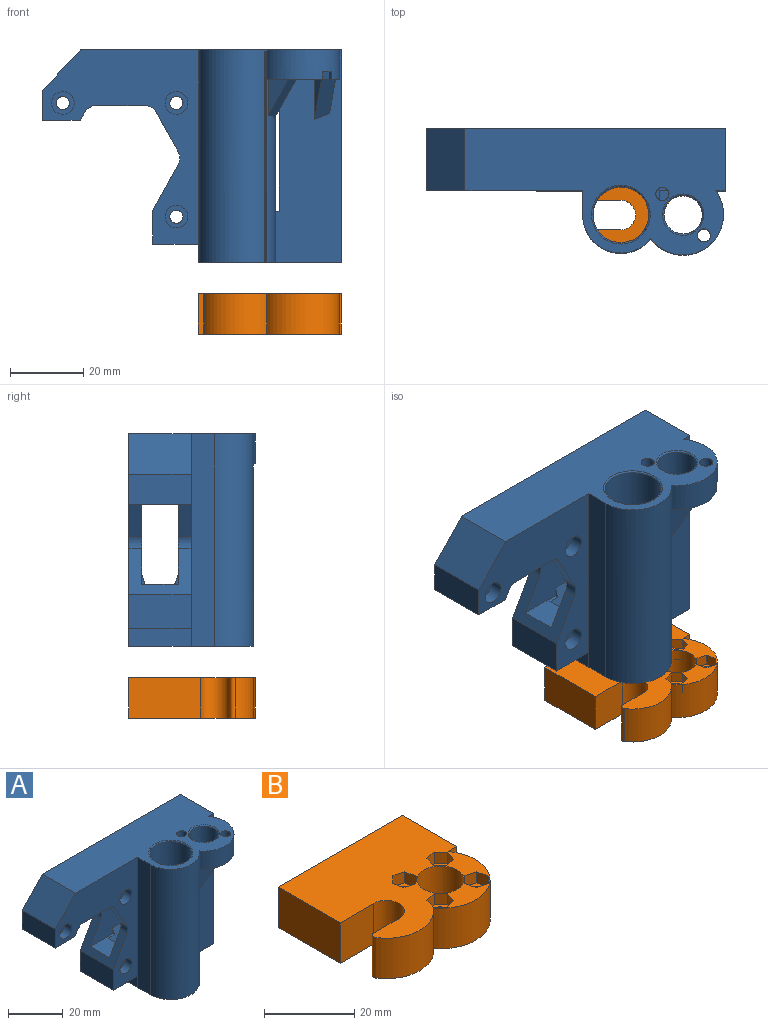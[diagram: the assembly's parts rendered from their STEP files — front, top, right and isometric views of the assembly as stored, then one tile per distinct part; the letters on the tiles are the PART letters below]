
ASSEMBLY  parts=2 mates=1
PART A: 108 faces, bbox 81.5x34.5x58 mm
  f0: cylinder r=10.47mm len=50mm, axis (0,0,1), area 313.5mm2, adj f1,f3,f9,f82,f83,f87,f106
  f1: plane 39x33.98mm, normal (0,0,-1), area 786.5mm2, adj f0,f2,f4,f9,f11,f12,f21,f33
  f2: cylinder r=7.62mm len=57.6mm, axis (0,0,1), area 2698.4mm2, adj f1,f79,f105,f106,f107
  f3: plane 15.16x13.29mm, normal (0,0,-1), area 49.7mm2, adj f0,f5,f9,f80,f82,f83,f87,f89
  f4: plane 58x18.03mm, normal (0,-1,0), area 843.5mm2, adj f1,f5,f8,f9,f10,f21,f37,f38
  f5: cylinder r=11mm len=19.83mm, axis (0,0,1), area 268.6mm2, adj f3,f4,f8,f10,f11,f96,f100,f101
  f6: cylinder r=1.8mm len=6mm, axis (0,0,1), area 67.9mm2, adj f10,f101
  f7: cylinder r=1.8mm len=6mm, axis (0,0,1), area 67.9mm2, adj f10,f90
  f8: plane 13.23x12.97mm, normal (0,0,-1), area 41.4mm2, adj f4,f5,f80,f84,f85,f86,f88,f98
  f9: plane 50x6.5mm, normal (1,0,0), area 316.8mm2, adj f0,f1,f3,f4,f89,f95,f102,f103
  f10: plane 71.05x34.5mm, normal (0,0,1), area 1473.5mm2, adj f4,f5,f6,f7,f11,f12,f21,f34
  f11: cylinder r=10.47mm len=58mm, axis (0,0,1), area 1440.2mm2, adj f1,f5,f10,f78,f105,f107
  f12: plane 58x42.53mm, normal (0,-1,0), area 907.7mm2, adj f1,f10,f13,f14,f15,f27,f28,f29
  f13: plane 17x11.05mm, normal (-0.87,0,-0.49), area 116.3mm2, adj f12,f14,f29,f30,f42,f57,f60,f75
  f14: cylinder r=3.5mm len=3.5mm, axis (0,1,0), area 12.4mm2, adj f12,f13,f15,f57
  f15: plane 17x12.59mm, normal (-0.87,0,0.49), area 132.8mm2, adj f12,f14,f30,f31,f42,f57,f60,f76
  f16: plane 10x3.25mm, normal (1,0,0), area 23.1mm2, adj f38,f55,f56,f57,f60,f75
  f17: plane 30.15x0.91mm, normal (0,0.71,0.71), area 36.2mm2, adj f18,f20,f21,f70,f71
  f18: plane 30.11x2.39mm, normal (0,0,1), area 70.9mm2, adj f17,f19,f21,f70
  f19: plane 30.15x0.91mm, normal (0,-0.71,0.71), area 36.2mm2, adj f18,f20,f21,f70,f71
  f20: cylinder r=4.07mm len=29.1mm, axis (1,0,0), area 618.8mm2, adj f17,f19,f21,f71
  f21: plane 58x17mm, normal (1,0,0), area 620mm2, adj f1,f4,f10,f17,f18,f19,f20,f38
  f22: plane 28x6.57mm, normal (1,0,0), area 108.5mm2, adj f38,f40,f42,f55,f59,f60
  f23: plane 28x6.57mm, normal (-1,0,0), area 108.5mm2, adj f38,f40,f42,f49,f50,f51
  f24: cylinder r=1.8mm len=13.5mm, axis (0,1,0), area 152.7mm2, adj f42,f48
  f25: cylinder r=1.8mm len=13.5mm, axis (0,1,0), area 152.7mm2, adj f42,f46
  f26: cylinder r=1.8mm len=13.5mm, axis (0,1,0), area 152.7mm2, adj f42,f44
  f27: plane 17x1.73mm, normal (0.5,0,-0.87), area 34mm2, adj f12,f28,f41,f42
  f28: plane 17x14.58mm, normal (0,0,-1), area 247.8mm2, adj f12,f27,f29,f42
  f29: cylinder r=3mm len=17mm, axis (0,1,0), area 54.2mm2, adj f12,f13,f28,f42
  f30: cylinder r=3.5mm len=3.5mm, axis (0,1,0), area 12.4mm2, adj f13,f15,f42,f60
  f31: plane 17x9.14mm, normal (-1,0,0), area 155.4mm2, adj f12,f15,f32,f42
  f32: plane 17x12.5mm, normal (0,0,-1), area 212.5mm2, adj f12,f31,f33,f42
  f33: plane 17x5mm, normal (-1,0,0), area 85mm2, adj f1,f12,f32,f42
  f34: plane 17x10.95mm, normal (-0.72,0,0.69), area 257.3mm2, adj f10,f12,f35,f42
  f35: plane 17x8.3mm, normal (-1,0,0), area 141.1mm2, adj f12,f34,f36,f42
  f36: plane 17x10.21mm, normal (0,0,-1), area 173.6mm2, adj f12,f35,f41,f42
  f37: plane 28x6.57mm, normal (1,0,0), area 108.5mm2, adj f4,f38,f40,f56,f57,f58
  f38: plane 41.5x17mm, normal (0,0,-1), area 173.3mm2, adj f4,f16,f21,f22,f23,f37,f39,f42
  f39: plane 28x6.57mm, normal (-1,0,0), area 108.5mm2, adj f4,f38,f40,f52,f53,f54
  f40: plane 41.5x17mm, normal (0,0,1), area 256.4mm2, adj f4,f21,f22,f23,f37,f39,f42,f50
  f41: plane 17x2.97mm, normal (0.87,0,-0.5), area 58.3mm2, adj f12,f27,f36,f42
  f42: plane 81.5x58mm, normal (0,1,0), area 3200.2mm2, adj f1,f10,f13,f15,f21,f22,f23,f24
  f43: cylinder r=3.1mm len=6.2mm, axis (0,-1,0), area 68.2mm2, adj f12,f44
  f44: plane 6.2x6.2mm, normal (0,-1,0), area 20mm2, adj f26,f43
  f45: cylinder r=3.1mm len=6.2mm, axis (0,-1,0), area 68.2mm2, adj f12,f46
  f46: plane 6.2x6.2mm, normal (0,-1,0), area 20mm2, adj f25,f45
  f47: cylinder r=3.1mm len=6.2mm, axis (0,-1,0), area 68.2mm2, adj f12,f48
  f48: plane 6.2x6.2mm, normal (0,-1,0), area 20mm2, adj f24,f47
  f49: plane 19.31x17mm, normal (0,-1,0), area 328.3mm2, adj f21,f23,f50,f51
  f50: plane 17x5.62mm, normal (0,-0.94,0.34), area 101.7mm2, adj f21,f23,f40,f49
  f51: plane 17x3.07mm, normal (0,-0.71,-0.71), area 73.8mm2, adj f21,f23,f38,f49
  f52: plane 17x5.62mm, normal (0,0.94,0.34), area 101.7mm2, adj f21,f39,f40,f53
  f53: plane 19.31x17mm, normal (0,1,0), area 328.3mm2, adj f21,f39,f52,f54
  f54: plane 17x3.07mm, normal (0,0.71,-0.71), area 73.8mm2, adj f21,f38,f39,f53
  f55: plane 23.5x3.07mm, normal (0,-0.71,-0.71), area 102mm2, adj f16,f22,f38,f60
  f56: plane 23.5x3.07mm, normal (0,0.71,-0.71), area 102mm2, adj f16,f37,f38,f57
  f57: plane 31.95x22mm, normal (0,1,0), area 573.5mm2, adj f13,f14,f15,f16,f37,f56,f58,f74
  f58: plane 23.5x5.62mm, normal (0,0.94,0.34), area 131.9mm2, adj f37,f40,f57,f61,f74,f76
  f59: plane 23.5x5.62mm, normal (0,-0.94,0.34), area 131.9mm2, adj f22,f40,f60,f61,f76,f77
  f60: plane 31.95x22mm, normal (0,-1,0), area 573.5mm2, adj f13,f15,f16,f22,f30,f55,f59,f75
  f61: plane 8.04x2.93mm, normal (1,0,0), area 20.4mm2, adj f40,f58,f59,f76
  f62: plane 30.15x0.91mm, normal (0,0.71,0.71), area 36.2mm2, adj f21,f63,f65,f66,f67
  f63: plane 30.11x2.39mm, normal (0,0,1), area 70.9mm2, adj f21,f62,f64,f66
  f64: plane 30.15x0.91mm, normal (0,-0.71,0.71), area 36.2mm2, adj f21,f63,f65,f66,f67
  f65: cylinder r=4.07mm len=29.1mm, axis (1,0,0), area 618.8mm2, adj f21,f62,f64,f67
  f66: cone r=5mm half-angle=13.6deg, axis (-1,0,0), area 85.3mm2, adj f62,f63,f64,f67,f68
  f67: plane 8.6x8.3mm, normal (-1,0,0), area 5.1mm2, adj f62,f64,f65,f66
  f68: cylinder r=5mm len=10mm, axis (-1,0,0), area 157.1mm2, adj f66,f69
  f69: plane 10x10mm, normal (1,0,0), area 78.5mm2, adj f68
  f70: cone r=5mm half-angle=13.6deg, axis (-1,0,0), area 85.3mm2, adj f17,f18,f19,f71,f72
  f71: plane 8.6x8.3mm, normal (-1,0,0), area 5.1mm2, adj f17,f19,f20,f70
  f72: cylinder r=5mm len=10mm, axis (1,0,0), area 157.1mm2, adj f70,f73
  f73: plane 10x10mm, normal (1,0,0), area 78.5mm2, adj f72
  f74: plane 2.69x0.98mm, normal (-1,0,0), area 1.3mm2, adj f57,f58,f76
  f75: plane 10x7.79mm, normal (0,0,-1), area 77.9mm2, adj f13,f16,f57,f60
  f76: plane 11.45x10mm, normal (0,0,1), area 90.3mm2, adj f15,f57,f58,f59,f60,f61,f74,f77
  f77: plane 2.69x0.98mm, normal (-1,0,0), area 1.3mm2, adj f59,f60,f76
  f78: plane 58x6.5mm, normal (-1,0,0), area 377mm2, adj f1,f10,f11,f12
  f79: torus R=8.01mm, axis (0,0,-1), area 30.6mm2, adj f2,f10
  f80: cylinder r=5.25mm len=10.5mm, axis (0,0,1), area 228.4mm2, adj f3,f8,f81,f88,f89,f90,f97,f98
  f81: torus R=5.65mm, axis (0,0,-1), area 21.3mm2, adj f10,f80
  f82: plane 10.65x6.01mm, normal (0.53,0.85,0), area 37.8mm2, adj f0,f3,f87
  f83: plane 9.83x5.55mm, normal (-0.53,-0.85,0), area 32.2mm2, adj f0,f3,f87
  f84: plane 10.95x7.05mm, normal (-0.97,-0.26,0), area 40mm2, adj f4,f8,f86
  f85: plane 9.35x6.02mm, normal (0.97,0.26,0), area 29.1mm2, adj f4,f8,f86
  f86: plane 10.95x7.05mm, normal (0.22,-0.8,-0.55), area 48.8mm2, adj f4,f8,f84,f85
  f87: plane 10.65x7.67mm, normal (0.7,-0.44,-0.55), area 48.3mm2, adj f0,f3,f82,f83
  f88: plane 3x2.27mm, normal (-0.5,-0.87,0), area 5.3mm2, adj f4,f8,f80,f90,f94,f95
  f89: plane 3x2.24mm, normal (0.87,0.5,0), area 5.2mm2, adj f3,f9,f80,f90,f91,f95
  f90: plane 8.93x8.9mm, normal (0,0,-1), area 24.8mm2, adj f7,f80,f88,f89,f91,f92,f93,f94
  f91: plane 3x2.44mm, normal (0.71,0.71,0), area 10.3mm2, adj f89,f90,f92,f95
  f92: plane 3.33x3mm, normal (0.97,-0.26,0), area 10.4mm2, adj f90,f91,f93,f95
  f93: plane 3.33x3mm, normal (0.26,-0.97,0), area 10.4mm2, adj f90,f92,f94,f95
  f94: plane 3x2.44mm, normal (-0.71,-0.71,0), area 10.3mm2, adj f88,f90,f93,f95
  f95: plane 6.76x6.7mm, normal (0,0,1), area 17.2mm2, adj f4,f9,f88,f89,f91,f92,f93,f94
  f96: plane 3.21x2mm, normal (0.3,0.95,0), area 6.7mm2, adj f3,f5,f97,f101
  f97: plane 3.31x2mm, normal (0.98,0.22,0), area 6.8mm2, adj f3,f80,f96,f101
  f98: plane 2x0.35mm, normal (0.68,-0.74,0), area 0.9mm2, adj f8,f80,f99,f101
  f99: plane 3.29x2mm, normal (-0.3,-0.95,0), area 6.9mm2, adj f8,f98,f100,f101
  f100: plane 3.14x2mm, normal (-0.98,-0.22,0), area 6.4mm2, adj f5,f8,f99,f101
  f101: plane 6.71x6.52mm, normal (0,0,-1), area 20.1mm2, adj f5,f6,f80,f96,f97,f98,f99,f100
  f102: plane 4.43x3.97mm, normal (0.67,-0.74,0), area 5.9mm2, adj f4,f9,f103,f104
  f103: plane 4.43x3.97mm, normal (0,0,-1), area 8.8mm2, adj f4,f9,f102
  f104: plane 4.43x3.97mm, normal (0,0,1), area 8.8mm2, adj f4,f9,f102
  f105: plane 57.5x2.15mm, normal (0.66,0.75,0), area 164.7mm2, adj f1,f2,f11,f107
  f106: plane 57.5x2.15mm, normal (-0.66,-0.75,0), area 164.7mm2, adj f0,f1,f2,f5,f107
  f107: plane 2.81x2.65mm, normal (0,0,-1), area 2.9mm2, adj f2,f11,f105,f106
PART B: 45 faces, bbox 39x34.5x11 mm
  f0: plane 5.84x5.75mm, normal (0,0,1), area 13.2mm2, adj f15,f25,f26,f27,f28,f29,f40
  f1: plane 5.84x5.75mm, normal (0,0,1), area 13.2mm2, adj f18,f30,f31,f32,f33,f34,f41
  f2: plane 5.84x5.75mm, normal (0,0,1), area 13.2mm2, adj f14,f35,f36,f37,f38,f39,f42
  f3: plane 5.84x5.75mm, normal (0,0,1), area 13.2mm2, adj f13,f20,f21,f22,f23,f24,f43
  f4: plane 11x10.48mm, normal (0.01,-1,0), area 115.2mm2, adj f5,f17,f19,f44
  f5: cylinder r=4.05mm len=11mm, axis (0,0,1), area 140mm2, adj f4,f6,f19,f44
  f6: plane 11x8.02mm, normal (0,1,0), area 88.2mm2, adj f5,f7,f19,f44
  f7: cylinder r=1mm len=11mm, axis (0,0,1), area 23.5mm2, adj f6,f8,f19,f44
  f8: cylinder r=10.47mm len=17.03mm, axis (0,0,1), area 219.3mm2, adj f7,f9,f19,f44
  f9: cylinder r=11mm len=19.83mm, axis (0,0,1), area 379.3mm2, adj f8,f10,f19,f44
  f10: plane 11x2.65mm, normal (0,-1,0), area 29.2mm2, adj f9,f11,f19,f44
  f11: plane 17x11mm, normal (1,0,0), area 187mm2, adj f10,f12,f19,f44
  f12: plane 39x11mm, normal (0,1,0), area 429mm2, adj f11,f17,f19,f44
  f13: cylinder r=1.8mm len=8mm, axis (0,0,1), area 90.5mm2, adj f3,f19
  f14: cylinder r=1.8mm len=8mm, axis (0,0,1), area 90.5mm2, adj f2,f19
  f15: cylinder r=1.8mm len=8mm, axis (0,0,1), area 90.5mm2, adj f0,f19
  f16: cylinder r=5.25mm len=11mm, axis (0,0,1), area 362.9mm2, adj f19,f44
  f17: plane 19.54x11mm, normal (-1,0,0), area 214.9mm2, adj f4,f12,f19,f44
  f18: cylinder r=1.8mm len=8mm, axis (0,0,1), area 90.5mm2, adj f1,f19
  f19: plane 39x34.5mm, normal (0,0,-1), area 1014.1mm2, adj f4,f5,f6,f7,f8,f9,f10,f11
  f20: plane 3x2.18mm, normal (-0.73,-0.69,0), area 9mm2, adj f3,f21,f43,f44
  f21: plane 3x2.87mm, normal (-0.96,0.29,0), area 9mm2, adj f3,f20,f22,f44
  f22: plane 3x2.92mm, normal (-0.23,0.97,0), area 9mm2, adj f3,f21,f23,f44
  f23: plane 3x2.18mm, normal (0.73,0.69,0), area 9mm2, adj f3,f22,f24,f44
  f24: plane 3x2.87mm, normal (0.96,-0.29,0), area 9mm2, adj f3,f23,f43,f44
  f25: plane 3x2.18mm, normal (0.73,0.69,0), area 9mm2, adj f0,f26,f40,f44
  f26: plane 3x2.87mm, normal (0.96,-0.29,0), area 9mm2, adj f0,f25,f27,f44
  f27: plane 3x2.92mm, normal (0.23,-0.97,0), area 9mm2, adj f0,f26,f28,f44
  f28: plane 3x2.18mm, normal (-0.73,-0.69,0), area 9mm2, adj f0,f27,f29,f44
  f29: plane 3x2.87mm, normal (-0.96,0.29,0), area 9mm2, adj f0,f28,f40,f44
  f30: plane 3x2.18mm, normal (0.69,-0.73,0), area 9mm2, adj f1,f31,f41,f44
  f31: plane 3x2.87mm, normal (-0.29,-0.96,0), area 9mm2, adj f1,f30,f32,f44
  f32: plane 3x2.92mm, normal (-0.97,-0.23,0), area 9mm2, adj f1,f31,f33,f44
  f33: plane 3x2.18mm, normal (-0.69,0.73,0), area 9mm2, adj f1,f32,f34,f44
  f34: plane 3x2.87mm, normal (0.29,0.96,0), area 9mm2, adj f1,f33,f41,f44
  f35: plane 3x2.18mm, normal (-0.69,0.73,0), area 9mm2, adj f2,f36,f42,f44
  f36: plane 3x2.87mm, normal (0.29,0.96,0), area 9mm2, adj f2,f35,f37,f44
  f37: plane 3x2.92mm, normal (0.97,0.23,0), area 9mm2, adj f2,f36,f38,f44
  f38: plane 3x2.18mm, normal (0.69,-0.73,0), area 9mm2, adj f2,f37,f39,f44
  f39: plane 3x2.87mm, normal (-0.29,-0.96,0), area 9mm2, adj f2,f38,f42,f44
  f40: plane 3x2.92mm, normal (-0.23,0.97,0), area 9mm2, adj f0,f25,f29,f44
  f41: plane 3x2.92mm, normal (0.97,0.23,0), area 9mm2, adj f1,f30,f34,f44
  f42: plane 3x2.92mm, normal (-0.97,-0.23,0), area 9mm2, adj f2,f35,f39,f44
  f43: plane 3x2.92mm, normal (0.23,-0.97,0), area 9mm2, adj f3,f20,f24,f44
  f44: plane 39x34.5mm, normal (0,0,1), area 961.2mm2, adj f4,f5,f6,f7,f8,f9,f10,f11
PLACE A t=(-4.92,15.93,-2.38)mm fixed
PLACE B t=(4.5,-3.6,-46.44)mm
MATE slider A.f1 <-> B.f44  axis (0,0,-1) through (-8.38,15.93,-34.89)mm
